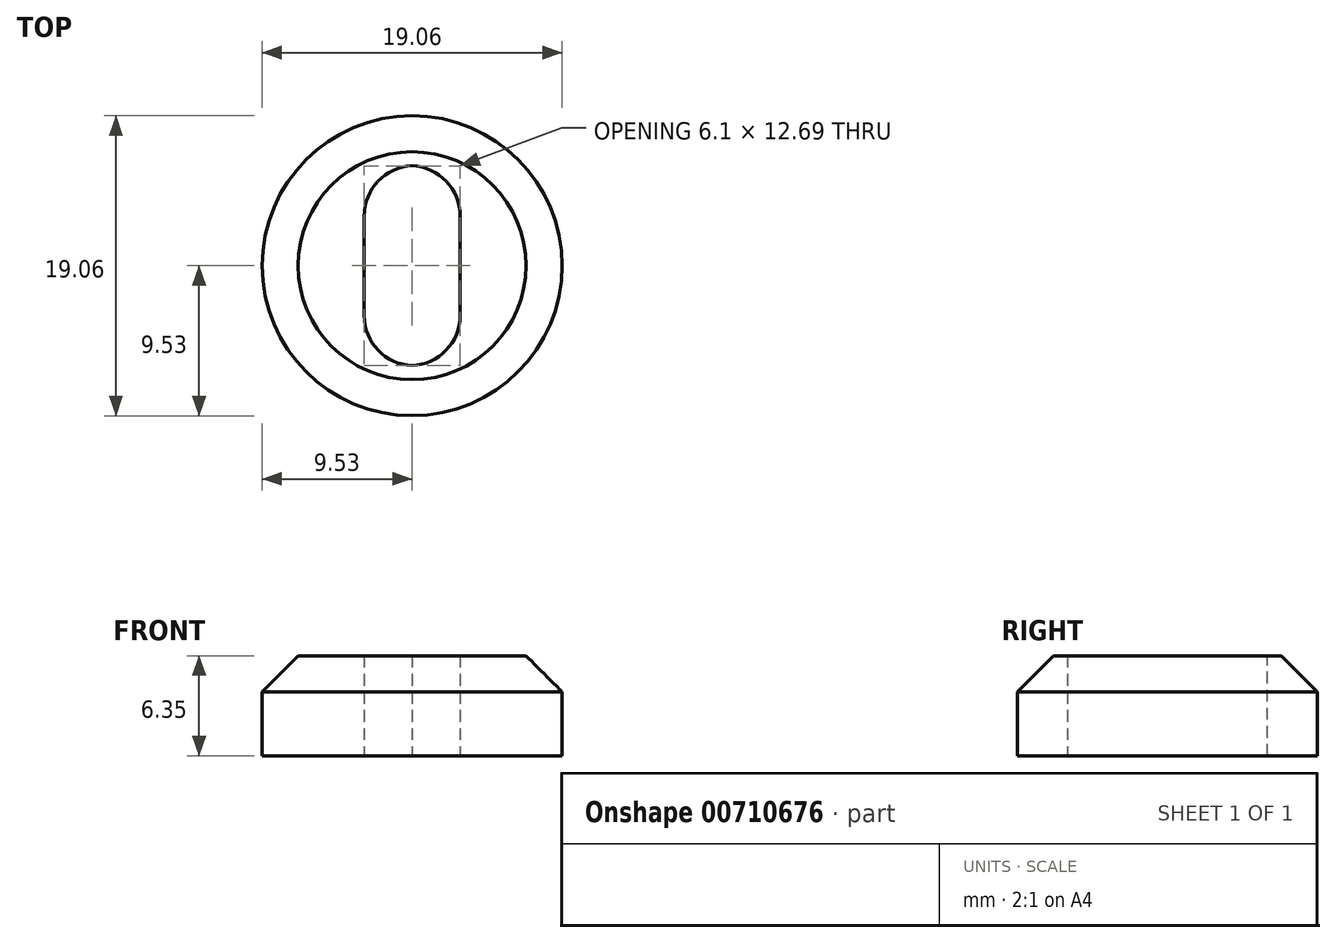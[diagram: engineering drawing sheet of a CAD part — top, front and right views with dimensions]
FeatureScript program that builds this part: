
annotation { "Feature Type Name" : "Feature", "Feature Type Description" : "" }
export const myFeature = defineFeature(function(context is Context, id is Id, definition is map)
    precondition{}
    {
        {
            var Q0;
            Q0=qCreatedBy(makeId("Top.planeOp"),FACE);
            var sketch = newSketch(context, id + "F0", { "sketchPlane" : qUnion([Q0])});
            skCircle(sketch, "E0", {"center": v(0, 0) * mm, "radius": 9.53 * mm});
            skLineSegment(sketch, "E1.bottom", {"start": v(3.05, 6.35) * mm, "end": v(-3.05, 6.35) * mm});
            skLineSegment(sketch, "E1.top", {"start": v(3.05, -6.35) * mm, "end": v(-3.05, -6.35) * mm});
            skLineSegment(sketch, "E1.left", {"start": v(3.05, 6.35) * mm, "end": v(3.05, -6.35) * mm});
            skLineSegment(sketch, "E1.right", {"start": v(-3.05, 6.35) * mm, "end": v(-3.05, -6.35) * mm});
            skSolve(sketch);
        }
        {
            var Q0;
            Q0=makeQuery(id+"F0.imprint","IMPRINT",FACE,{"disambiguationData":[TD([[makeQuery(id+"F0.imprint","IMPRINT",EDGE,{"derivedFrom":sQuery(id+"F0.wireOp",EDGE,"E0")}),1.0]])]});
            extrude(context, id + "F1", {"entities" : qUnion([Q0]), "depth" : 6.35 * mm, "offsetDistance" : 25.4 * mm});
        }
        {
            var Q0;
            Q0=makeQuery(id+"F1.opExtrude","SWEPT_EDGE",EDGE,{"disambiguationData":[OSD([sQuery(id+"F0.wireOp",EDGE,"E1.bottom"),sQuery(id+"F0.wireOp",EDGE,"E1.right")])]});
            var Q1;
            Q1=makeQuery(id+"F1.opExtrude","SWEPT_EDGE",EDGE,{"disambiguationData":[OSD([sQuery(id+"F0.wireOp",EDGE,"E1.bottom"),sQuery(id+"F0.wireOp",EDGE,"E1.left")])]});
            var Q2;
            Q2=makeQuery(id+"F1.opExtrude","SWEPT_EDGE",EDGE,{"disambiguationData":[OSD([sQuery(id+"F0.wireOp",EDGE,"E1.top"),sQuery(id+"F0.wireOp",EDGE,"E1.right")])]});
            var Q3;
            Q3=makeQuery(id+"F1.opExtrude","SWEPT_EDGE",EDGE,{"disambiguationData":[OSD([sQuery(id+"F0.wireOp",EDGE,"E1.top"),sQuery(id+"F0.wireOp",EDGE,"E1.left")])]});
            fillet(context, id + "F2", {"entities" : qUnion([Q0, Q1, Q2, Q3]), "radius" : 3.19 * mm, "tangentPropagation" : true, "allowEdgeOverflow" : false});
        }
        {
            var Q0;
            Q0=makeQuery(id+"F1.opExtrude","CAP_EDGE",EDGE,{"disambiguationData":[OSD([sQuery(id+"F0.wireOp",EDGE,"E0")])],"isStart":false});
            chamfer(context, id + "F3", {"entities" : qUnion([Q0]), "width" : 2.3 * mm, "tangentPropagation" : true});
        }
    });
